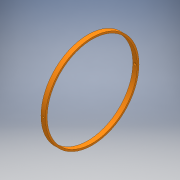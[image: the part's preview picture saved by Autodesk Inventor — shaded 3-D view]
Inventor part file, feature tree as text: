
AUTODESK INVENTOR PART (.ipt)
format: ipt  version: 2018 (Build 220112000, 112)  size: 138,752 bytes
history: native  units: mm
features: extrude x3, sketch x3, plane x2, mirror x1, projected_geometry x1
ambient origin geometry x8: Origin, YZ Plane, XZ Plane, XY Plane, X Axis, Y Axis, Z Axis, Center Point
bodies: Solid1 (feature_tree)
feature tree (10):
  extrude  "Extrusion1"  Depth=204.0mm
  plane  "Work Plane1"
  extrude  "Extrusion2"  Depth=10.0mm
  plane  "Work Plane2"
  extrude  "Extrusion3"  Depth=6.0mm
  mirror  "Mirror1"
  sketch  "Sketch1"  dims[d0=212.0mm d1=204.0mm]
  sketch  "Sketch2"  dims[d2=10.0mm d3=0.0mm d4=4.0mm]
  projected_geometry  "Projected Loop1"
  sketch  "Sketch3"  dims[d5=227.25mm d6=0.0mm d7=6.0mm d8=5.0mm d9=0.0mm]
